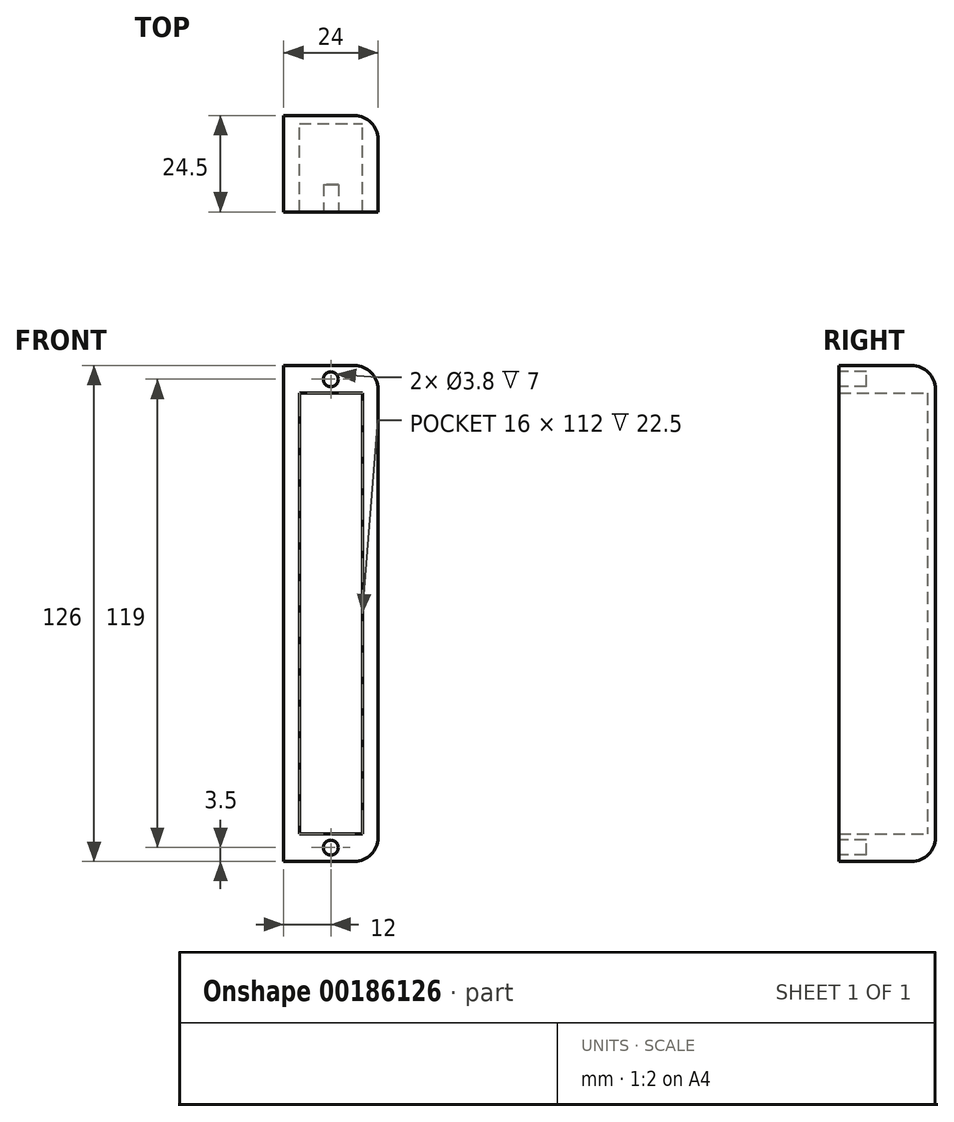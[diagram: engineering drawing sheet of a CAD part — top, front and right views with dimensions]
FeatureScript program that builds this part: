
annotation { "Feature Type Name" : "Feature", "Feature Type Description" : "" }
export const myFeature = defineFeature(function(context is Context, id is Id, definition is map)
    precondition{}
    {
        {
            var Q0;
            Q0=qCreatedBy(makeId("Front.planeOp"),FACE);
            var sketch = newSketch(context, id + "F0", { "sketchPlane" : qUnion([Q0])});
            skLineSegment(sketch, "E0.bottom", {"start": v(-12, 63) * mm, "end": v(12, 63) * mm});
            skLineSegment(sketch, "E0.top", {"start": v(-12, -63) * mm, "end": v(12, -63) * mm});
            skLineSegment(sketch, "E0.left", {"start": v(-12, 63) * mm, "end": v(-12, -63) * mm});
            skLineSegment(sketch, "E0.right", {"start": v(12, 63) * mm, "end": v(12, -63) * mm});
            skPoint(sketch, "E1", {"position": v(0, 63) * mm});
            skPoint(sketch, "E2", {"position": v(-12, 0) * mm});
            skLineSegment(sketch, "E3.bottom", {"start": v(-8, 56) * mm, "end": v(8, 56) * mm});
            skLineSegment(sketch, "E3.top", {"start": v(-8, -56) * mm, "end": v(8, -56) * mm});
            skLineSegment(sketch, "E3.left", {"start": v(-8, 56) * mm, "end": v(-8, -56) * mm});
            skLineSegment(sketch, "E3.right", {"start": v(8, 56) * mm, "end": v(8, -56) * mm});
            skPoint(sketch, "E4", {"position": v(0, 56) * mm});
            skPoint(sketch, "E5", {"position": v(8, 0) * mm});
            skSolve(sketch);
        }
        {
            var Q0;
            Q0=qSketchRegion(id+"F0",true);
            extrude(context, id + "F1", {"entities" : qUnion([Q0]), "depth" : 24.5 * mm});
        }
        {
            var Q0;
            Q0=makeQuery(id+"F0.imprint","IMPRINT",FACE,{"disambiguationData":[TD([[makeQuery(id+"F0.imprint","IMPRINT",EDGE,{"derivedFrom":sQuery(id+"F0.wireOp",EDGE,"E3.bottom")}),-1.0]])]});
            extrude(context, id + "F2", {"entities" : qUnion([Q0]), "operationType" : NewBodyOperationType.ADD, "depth" : 2 * mm});
        }
        {
            var Q0;
            Q0=makeQuery(id+"F1.opExtrude","CAP_FACE",FACE,{"disambiguationData":[OSD([sQuery(id+"F0.wireOp",EDGE,"E0.bottom"),sQuery(id+"F0.wireOp",EDGE,"E0.top"),sQuery(id+"F0.wireOp",EDGE,"E0.left"),sQuery(id+"F0.wireOp",EDGE,"E0.right"),sQuery(id+"F0.wireOp",EDGE,"E3.bottom"),sQuery(id+"F0.wireOp",EDGE,"E3.top"),sQuery(id+"F0.wireOp",EDGE,"E3.left"),sQuery(id+"F0.wireOp",EDGE,"E3.right")])],"isStart":false});
            var sketch = newSketch(context, id + "F3", { "sketchPlane" : qUnion([Q0])});
            skCircle(sketch, "E6", {"center": v(0, 59.5) * mm, "radius": 1.9 * mm});
            skCircle(sketch, "E7.MirrorC", {"center": v(0, -59.5) * mm, "radius": 1.9 * mm});
            skLineSegment(sketch, "E8", {"start": v(0, 63) * mm, "end": v(0, 56) * mm});
            skSolve(sketch);
        }
        {
            var Q0;
            Q0=qSketchRegion(id+"F3",true);
            extrude(context, id + "F4", {"entities" : qUnion([Q0]), "operationType" : NewBodyOperationType.REMOVE, "oppositeDirection" : true, "depth" : 7 * mm});
        }
        {
            var Q0;
            Q0=makeQuery(id+"F1.opExtrude","CAP_EDGE",EDGE,{"disambiguationData":[OSD([sQuery(id+"F0.wireOp",EDGE,"E0.bottom")])],"isStart":true});
            var Q1;
            Q1=makeQuery(id+"F1.opExtrude","CAP_EDGE",EDGE,{"disambiguationData":[OSD([sQuery(id+"F0.wireOp",EDGE,"E0.right")])],"isStart":true});
            var Q2;
            Q2=makeQuery(id+"F1.opExtrude","CAP_EDGE",EDGE,{"disambiguationData":[OSD([sQuery(id+"F0.wireOp",EDGE,"E0.top")])],"isStart":true});
            var Q3;
            Q3=makeQuery(id+"F1.opExtrude","SWEPT_EDGE",EDGE,{"disambiguationData":[OSD([sQuery(id+"F0.wireOp",EDGE,"E0.top"),sQuery(id+"F0.wireOp",EDGE,"E0.right")])]});
            var Q4;
            Q4=makeQuery(id+"F1.opExtrude","SWEPT_EDGE",EDGE,{"disambiguationData":[OSD([sQuery(id+"F0.wireOp",EDGE,"E0.bottom"),sQuery(id+"F0.wireOp",EDGE,"E0.right")])]});
            fillet(context, id + "F5", {"entities" : qUnion([Q0, Q1, Q2, Q3, Q4]), "radius" : 6 * mm, "tangentPropagation" : true, "allowEdgeOverflow" : false});
        }
    });
